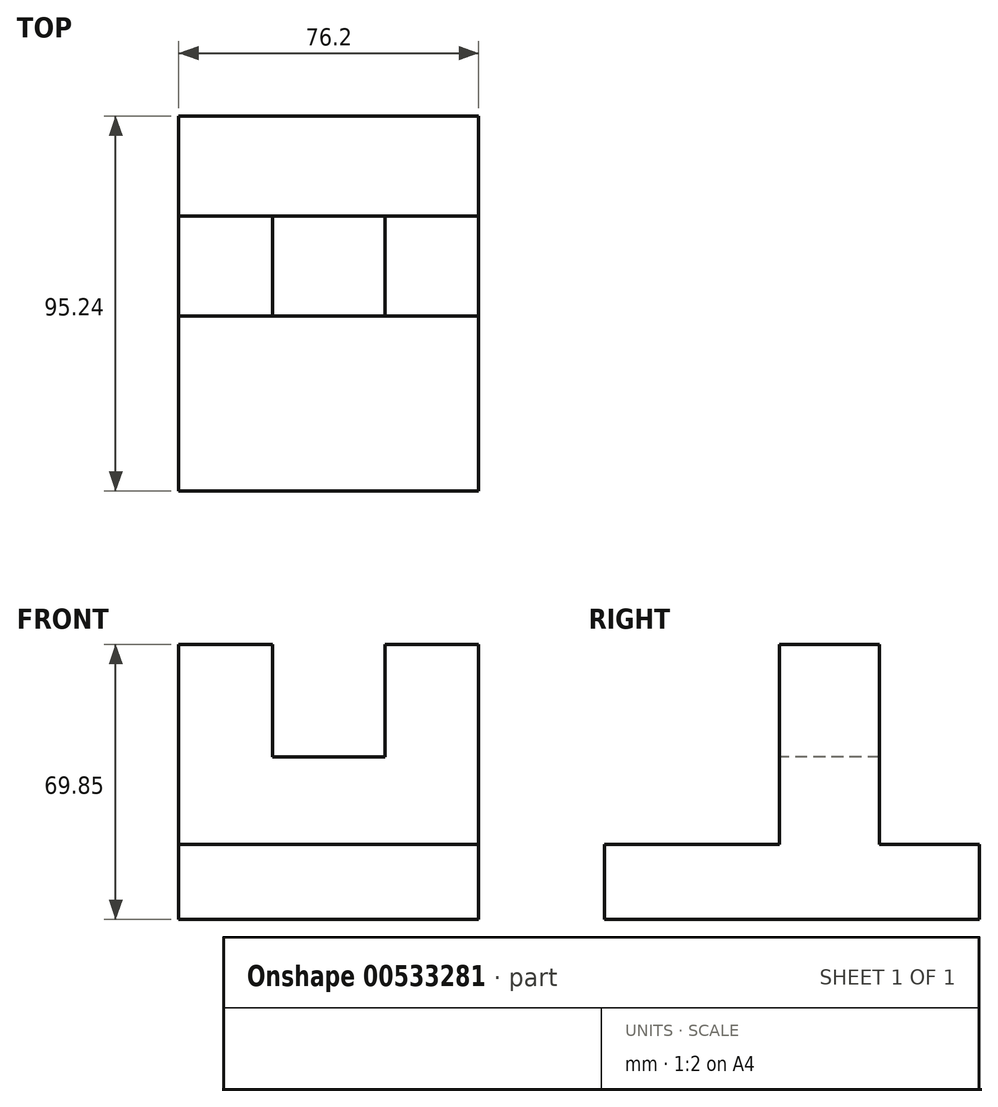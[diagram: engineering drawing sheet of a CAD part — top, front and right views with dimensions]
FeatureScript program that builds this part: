
annotation { "Feature Type Name" : "Feature", "Feature Type Description" : "" }
export const myFeature = defineFeature(function(context is Context, id is Id, definition is map)
    precondition{}
    {
        {
            var Q0;
            Q0=qCreatedBy(makeId("Top.planeOp"),FACE);
            var sketch = newSketch(context, id + "F0", { "sketchPlane" : qUnion([Q0])});
            skLineSegment(sketch, "E0.bottom", {"start": v(38.1, 47.63) * mm, "end": v(-38.1, 47.63) * mm});
            skLineSegment(sketch, "E0.top", {"start": v(38.1, -47.63) * mm, "end": v(-38.1, -47.63) * mm});
            skLineSegment(sketch, "E0.left", {"start": v(38.1, 47.63) * mm, "end": v(38.1, -47.63) * mm});
            skLineSegment(sketch, "E0.right", {"start": v(-38.1, 47.63) * mm, "end": v(-38.1, -47.63) * mm});
            skPoint(sketch, "E0.middle", {"position": v(0, 0) * mm});
            skSolve(sketch);
        }
        {
            var Q0;
            Q0 = qSketchRegion(id + "F0", true);
            extrude(context, id + "F1", {"entities" : qUnion([Q0]), "depth" : 19.05 * mm, "offsetDistance" : 25.4 * mm});
        }
        {
            var Q0;
            Q0=makeQuery(id+"F1.opExtrude","SWEPT_FACE",FACE,{"disambiguationData":[OSD([sQuery(id+"F0.wireOp",EDGE,"E0.left")])]});
            var sketch = newSketch(context, id + "F2", { "sketchPlane" : qUnion([Q0])});
            skLineSegment(sketch, "E1.bottom", {"start": v(-3.18, 19.05) * mm, "end": v(22.22, 19.05) * mm});
            skLineSegment(sketch, "E1.top", {"start": v(-3.18, 69.85) * mm, "end": v(22.22, 69.85) * mm});
            skLineSegment(sketch, "E1.left", {"start": v(-3.18, 19.05) * mm, "end": v(-3.18, 69.85) * mm});
            skLineSegment(sketch, "E1.right", {"start": v(22.22, 19.05) * mm, "end": v(22.22, 69.85) * mm});
            skSolve(sketch);
        }
        {
            var Q0;
            Q0=makeQuery(id+"F2.imprint","IMPRINT",FACE,{"disambiguationData":[TD([[makeQuery(id+"F2.imprint","IMPRINT",EDGE,{"derivedFrom":sQuery(id+"F2.wireOp",EDGE,"E1.bottom")}),-1.0]])]});
            var Q1;
            Q1=makeQuery(id+"F1.opExtrude","SWEPT_FACE",FACE,{"disambiguationData":[OSD([sQuery(id+"F0.wireOp",EDGE,"E0.right")])]});
            extrude(context, id + "F3", {"entities" : qUnion([Q0]), "operationType" : NewBodyOperationType.ADD, "endBound" : BoundingType.UP_TO_SURFACE, "oppositeDirection" : true, "depth" : 52.32 * mm, "endBoundEntityFace" : qUnion([Q1]), "offsetDistance" : 25.4 * mm});
        }
        {
            var Q0;
            {var subQ0=sQuery(id+"F0.wireOp",EDGE,"E0.right");var subQ1=sQuery(id+"F0.wireOp",EDGE,"E0.left");var subQ2=sQuery(id+"F0.wireOp",EDGE,"E0.bottom");Q0=makeQuery(id+"F3.boolean.opBoolean","SPLIT",FACE,{"disambiguationData":[TD([makeQuery(id+"F1.opExtrude","SWEPT_FACE",FACE,{"disambiguationData":[OSD([subQ2])]})])],"derivedFrom":makeQuery(id+"F1.opExtrude","CAP_FACE",FACE,{"disambiguationData":[OSD([subQ2,sQuery(id+"F0.wireOp",EDGE,"E0.top"),subQ1,subQ0])],"isStart":false})});}
            var sketch = newSketch(context, id + "F4", { "sketchPlane" : qUnion([Q0])});
            skCircle(sketch, "E2", {"center": v(-25.4, 34.93) * mm, "radius": 4.7 * mm});
            skSolve(sketch);
        }
        {
            var Q0;
            {var subQ0=sQuery(id+"F0.wireOp",EDGE,"E0.right");var subQ2=sQuery(id+"F0.wireOp",EDGE,"E0.left");var subQ3=sQuery(id+"F0.wireOp",EDGE,"E0.top");Q0=makeQuery(id+"F3.boolean.opBoolean","SPLIT",FACE,{"disambiguationData":[TD([makeQuery(id+"F1.opExtrude","SWEPT_FACE",FACE,{"disambiguationData":[OSD([subQ3])]})])],"derivedFrom":makeQuery(id+"F1.opExtrude","CAP_FACE",FACE,{"disambiguationData":[OSD([sQuery(id+"F0.wireOp",EDGE,"E0.bottom"),subQ3,subQ2,subQ0])],"isStart":false})});}
            var sketch = newSketch(context, id + "F5", { "sketchPlane" : qUnion([Q0])});
            skCircle(sketch, "E3", {"center": v(-25.4, -34.93) * mm, "radius": 4.7 * mm});
            skSolve(sketch);
        }
        {
            var Q0;
            Q0=makeQuery(id+"F3.opExtrude","SWEPT_FACE",FACE,{"disambiguationData":[OSD([sQuery(id+"F2.wireOp",EDGE,"E1.left")])]});
            var sketch = newSketch(context, id + "F6", { "sketchPlane" : qUnion([Q0])});
            skLineSegment(sketch, "E4", {"start": v(-14.29, 69.85) * mm, "end": v(-14.29, 41.27) * mm});
            skLineSegment(sketch, "E5", {"start": v(-14.29, 41.27) * mm, "end": v(14.29, 41.27) * mm});
            skLineSegment(sketch, "E6", {"start": v(14.29, 41.27) * mm, "end": v(14.29, 69.85) * mm});
            skSolve(sketch);
        }
        {
            var Q0;
            {var subQ0=sQuery(id+"F6.wireOp",EDGE,"E4");Q0=makeQuery(id+"F6.imprint","IMPRINT",FACE,{"disambiguationData":[TD([[makeQuery(id+"F6.imprint","IMPRINT",EDGE,{"derivedFrom":subQ0}),1.0]])]});}
            extrude(context, id + "F7", {"entities" : qUnion([Q0]), "operationType" : NewBodyOperationType.REMOVE, "oppositeDirection" : true, "depth" : 127 * mm, "offsetDistance" : 25.4 * mm});
        }
    });
